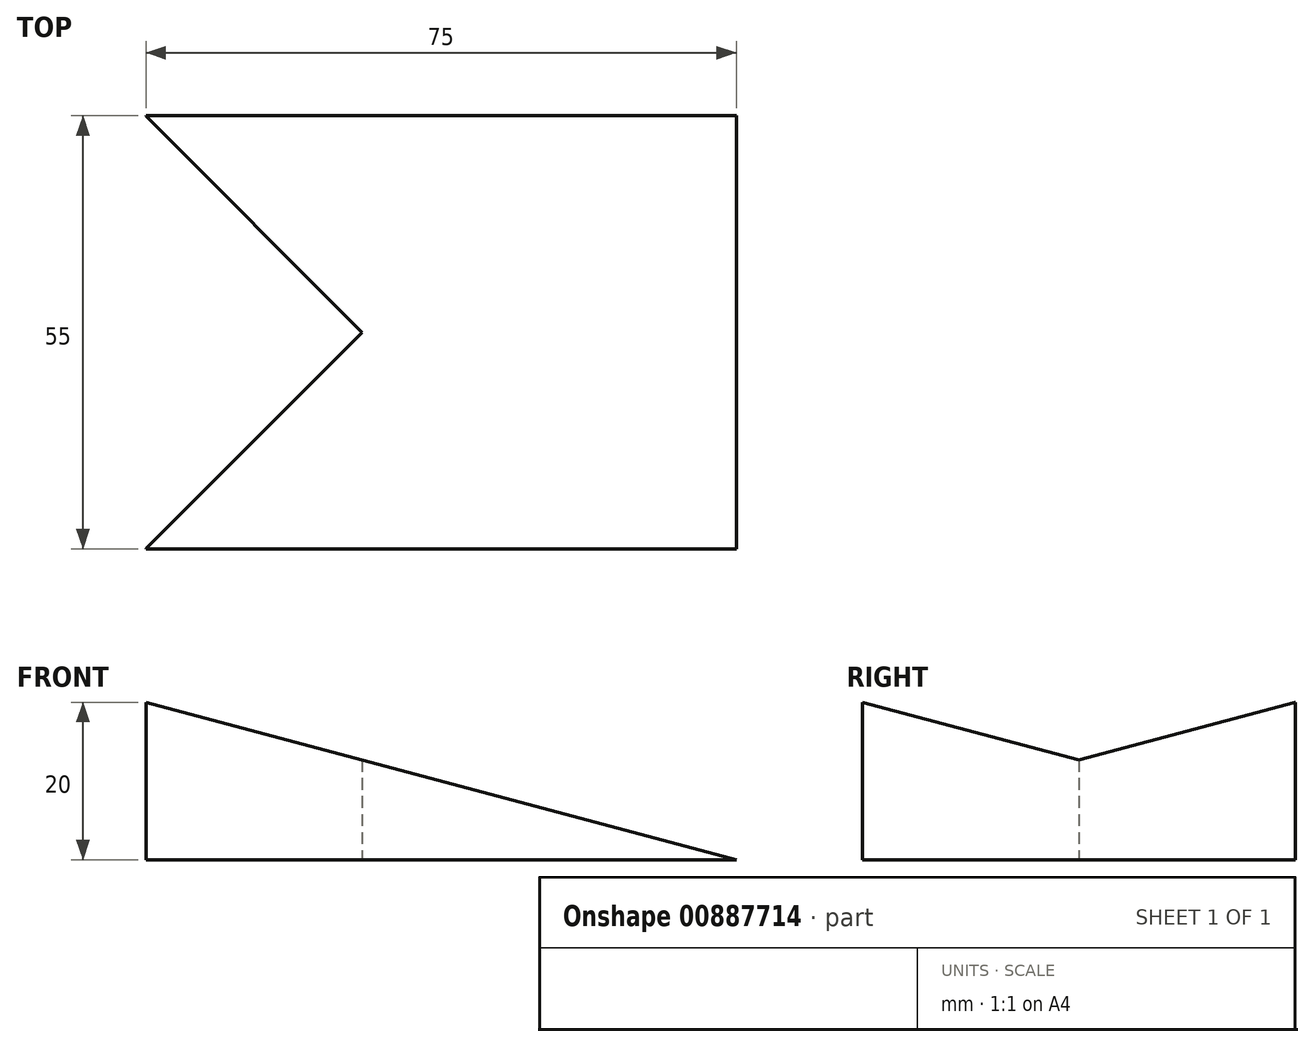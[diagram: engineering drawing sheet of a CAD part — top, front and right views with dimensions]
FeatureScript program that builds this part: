
annotation { "Feature Type Name" : "Feature", "Feature Type Description" : "" }
export const myFeature = defineFeature(function(context is Context, id is Id, definition is map)
    precondition{}
    {
        {
            var Q0;
            Q0=qCreatedBy(makeId("Front.planeOp"),FACE);
            var sketch = newSketch(context, id + "F0", { "sketchPlane" : qUnion([Q0])});
            skLineSegment(sketch, "E0", {"start": v(-22.45, 0) * mm, "end": v(-22.45, 20) * mm});
            skLineSegment(sketch, "E1", {"start": v(-22.45, 20) * mm, "end": v(52.55, 0) * mm});
            skLineSegment(sketch, "E2", {"start": v(52.55, 0) * mm, "end": v(-22.45, 0) * mm});
            skSolve(sketch);
        }
        {
            var Q0;
            Q0 = qSketchRegion(id + "F0", true);
            extrude(context, id + "F1", {"entities" : qUnion([Q0]), "depth" : 55 * mm, "offsetDistance" : 25 * mm});
        }
        {
            var Q0;
            Q0=qCreatedBy(makeId("Top.planeOp"),FACE);
            var sketch = newSketch(context, id + "F2", { "sketchPlane" : qUnion([Q0])});
            skLineSegment(sketch, "E3", {"start": v(-22.5, -55) * mm, "end": v(-22.5, 0) * mm});
            skLineSegment(sketch, "E4", {"start": v(-22.5, -55) * mm, "end": v(5, -27.5) * mm});
            skPoint(sketch, "E4.endSnap0", {"position": v(-22.5, -27.5) * mm});
            skLineSegment(sketch, "E5", {"start": v(5, -27.5) * mm, "end": v(-22.5, 0) * mm});
            skSolve(sketch);
        }
        {
            var Q0;
            Q0 = qSketchRegion(id + "F2", true);
            extrude(context, id + "F3", {"entities" : qUnion([Q0]), "operationType" : NewBodyOperationType.REMOVE, "depth" : 20 * mm, "offsetDistance" : 25 * mm});
        }
    });
